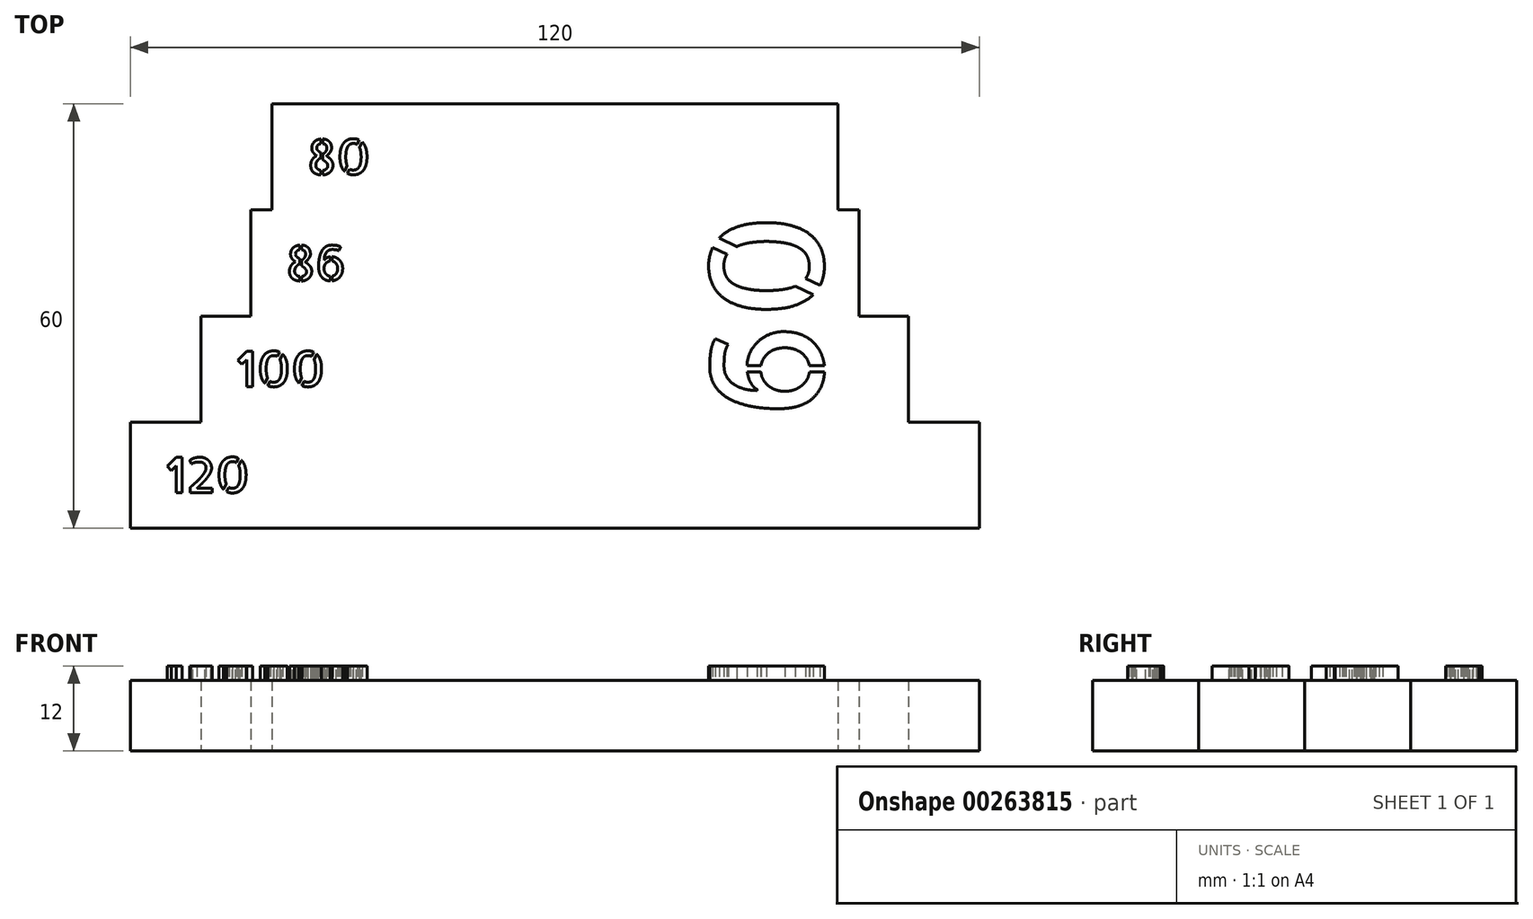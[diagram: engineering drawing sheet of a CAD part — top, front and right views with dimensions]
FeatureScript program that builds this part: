
annotation { "Feature Type Name" : "Feature", "Feature Type Description" : "" }
export const myFeature = defineFeature(function(context is Context, id is Id, definition is map)
    precondition{}
    {
        {
            var Q0;
            Q0=qCreatedBy(makeId("Top.planeOp"),FACE);
            var sketch = newSketch(context, id + "F0", { "sketchPlane" : qUnion([Q0])});
            skLineSegment(sketch, "E0.top", {"start": v(-60, 15) * mm, "end": v(60, 15) * mm});
            skLineSegment(sketch, "E0.left", {"start": v(-60, 0) * mm, "end": v(-60, 15) * mm});
            skLineSegment(sketch, "E0.right", {"start": v(60, 0) * mm, "end": v(60, 15) * mm});
            skLineSegment(sketch, "E1", {"start": v(60, 0) * mm, "end": v(-60, 0) * mm});
            skPoint(sketch, "E2.middle", {"position": v(0, 0) * mm});
            skPoint(sketch, "E3", {"position": v(0, 10) * mm});
            skPoint(sketch, "E4.endSnap0", {"position": v(0, 15) * mm});
            skPoint(sketch, "E5", {"position": v(-60, 7.5) * mm});
            skLineSegment(sketch, "E6.bottom", {"start": v(-50, 30) * mm, "end": v(50, 30) * mm});
            skLineSegment(sketch, "E6.top", {"start": v(-50, 15) * mm, "end": v(50, 15) * mm});
            skLineSegment(sketch, "E6.left", {"start": v(-50, 30) * mm, "end": v(-50, 15) * mm});
            skLineSegment(sketch, "E6.right", {"start": v(50, 30) * mm, "end": v(50, 15) * mm});
            skLineSegment(sketch, "E7.bottom", {"start": v(-43, 30) * mm, "end": v(43, 30) * mm});
            skLineSegment(sketch, "E7.top", {"start": v(-43, 45) * mm, "end": v(43, 45) * mm});
            skLineSegment(sketch, "E7.left", {"start": v(-43, 30) * mm, "end": v(-43, 45) * mm});
            skLineSegment(sketch, "E7.right", {"start": v(43, 30) * mm, "end": v(43, 45) * mm});
            skPoint(sketch, "E8", {"position": v(0, 30) * mm});
            skLineSegment(sketch, "E9.bottom", {"start": v(-40, 45) * mm, "end": v(40, 45) * mm});
            skLineSegment(sketch, "E9.top", {"start": v(-40, 60) * mm, "end": v(40, 60) * mm});
            skLineSegment(sketch, "E9.left", {"start": v(-40, 45) * mm, "end": v(-40, 60) * mm});
            skLineSegment(sketch, "E9.right", {"start": v(40, 45) * mm, "end": v(40, 60) * mm});
            skPoint(sketch, "E10", {"position": v(0, 45) * mm});
            skSolve(sketch);
        }
        {
            var Q0;
            Q0=qSketchRegion(id+"F0",true);
            extrude(context, id + "F1", {"entities" : qUnion([Q0]), "depth" : 10 * mm});
        }
        {
            var Q0;
            Q0=makeQuery(id+"F1.opExtrude","CAP_FACE",FACE,{"disambiguationData":[OSD([sQuery(id+"F0.wireOp",EDGE,"E0.top"),sQuery(id+"F0.wireOp",EDGE,"E0.left"),sQuery(id+"F0.wireOp",EDGE,"E0.right"),sQuery(id+"F0.wireOp",EDGE,"E2.bottom"),sQuery(id+"F0.wireOp",EDGE,"E2.top"),sQuery(id+"F0.wireOp",EDGE,"E2.left"),sQuery(id+"F0.wireOp",EDGE,"E2.right"),sQuery(id+"F0.wireOp",EDGE,"b55eea4f-ecd7-418c-8d86-c4403fabcb0e.sketch_text.stroke-0"),sQuery(id+"F0.wireOp",EDGE,"b55eea4f-ecd7-418c-8d86-c4403fabcb0e.sketch_text.stroke-1"),sQuery(id+"F0.wireOp",EDGE,"b55eea4f-ecd7-418c-8d86-c4403fabcb0e.sketch_text.stroke-2"),sQuery(id+"F0.wireOp",EDGE,"b55eea4f-ecd7-418c-8d86-c4403fabcb0e.sketch_text.stroke-3"),sQuery(id+"F0.wireOp",EDGE,"b55eea4f-ecd7-418c-8d86-c4403fabcb0e.sketch_text.stroke-4"),sQuery(id+"F0.wireOp",EDGE,"b55eea4f-ecd7-418c-8d86-c4403fabcb0e.sketch_text.stroke-5"),sQuery(id+"F0.wireOp",EDGE,"b55eea4f-ecd7-418c-8d86-c4403fabcb0e.sketch_text.stroke-6"),sQuery(id+"F0.wireOp",EDGE,"b55eea4f-ecd7-418c-8d86-c4403fabcb0e.sketch_text.stroke-7"),sQuery(id+"F0.wireOp",EDGE,"b55eea4f-ecd7-418c-8d86-c4403fabcb0e.sketch_text.stroke-8"),sQuery(id+"F0.wireOp",EDGE,"b55eea4f-ecd7-418c-8d86-c4403fabcb0e.sketch_text.stroke-9"),sQuery(id+"F0.wireOp",EDGE,"b55eea4f-ecd7-418c-8d86-c4403fabcb0e.sketch_text.stroke-10"),sQuery(id+"F0.wireOp",EDGE,"b55eea4f-ecd7-418c-8d86-c4403fabcb0e.sketch_text.stroke-11"),sQuery(id+"F0.wireOp",EDGE,"b55eea4f-ecd7-418c-8d86-c4403fabcb0e.sketch_text.stroke-12"),sQuery(id+"F0.wireOp",EDGE,"b55eea4f-ecd7-418c-8d86-c4403fabcb0e.sketch_text.stroke-13"),sQuery(id+"F0.wireOp",EDGE,"b55eea4f-ecd7-418c-8d86-c4403fabcb0e.sketch_text.stroke-14"),sQuery(id+"F0.wireOp",EDGE,"b55eea4f-ecd7-418c-8d86-c4403fabcb0e.sketch_text.stroke-15"),sQuery(id+"F0.wireOp",EDGE,"b55eea4f-ecd7-418c-8d86-c4403fabcb0e.sketch_text.stroke-16"),sQuery(id+"F0.wireOp",EDGE,"b55eea4f-ecd7-418c-8d86-c4403fabcb0e.sketch_text.stroke-17"),sQuery(id+"F0.wireOp",EDGE,"b55eea4f-ecd7-418c-8d86-c4403fabcb0e.sketch_text.stroke-18"),sQuery(id+"F0.wireOp",EDGE,"b55eea4f-ecd7-418c-8d86-c4403fabcb0e.sketch_text.stroke-19"),sQuery(id+"F0.wireOp",EDGE,"b55eea4f-ecd7-418c-8d86-c4403fabcb0e.sketch_text.stroke-20"),sQuery(id+"F0.wireOp",EDGE,"b55eea4f-ecd7-418c-8d86-c4403fabcb0e.sketch_text.stroke-21"),sQuery(id+"F0.wireOp",EDGE,"b55eea4f-ecd7-418c-8d86-c4403fabcb0e.sketch_text.stroke-22"),sQuery(id+"F0.wireOp",EDGE,"b55eea4f-ecd7-418c-8d86-c4403fabcb0e.sketch_text.stroke-23"),sQuery(id+"F0.wireOp",EDGE,"b55eea4f-ecd7-418c-8d86-c4403fabcb0e.sketch_text.stroke-24"),sQuery(id+"F0.wireOp",EDGE,"b55eea4f-ecd7-418c-8d86-c4403fabcb0e.sketch_text.stroke-25"),sQuery(id+"F0.wireOp",EDGE,"b55eea4f-ecd7-418c-8d86-c4403fabcb0e.sketch_text.stroke-26"),sQuery(id+"F0.wireOp",EDGE,"b55eea4f-ecd7-418c-8d86-c4403fabcb0e.sketch_text.stroke-27"),sQuery(id+"F0.wireOp",EDGE,"b55eea4f-ecd7-418c-8d86-c4403fabcb0e.sketch_text.stroke-28"),sQuery(id+"F0.wireOp",EDGE,"b55eea4f-ecd7-418c-8d86-c4403fabcb0e.sketch_text.stroke-29"),sQuery(id+"F0.wireOp",EDGE,"b55eea4f-ecd7-418c-8d86-c4403fabcb0e.sketch_text.stroke-30"),sQuery(id+"F0.wireOp",EDGE,"b55eea4f-ecd7-418c-8d86-c4403fabcb0e.sketch_text.stroke-31"),sQuery(id+"F0.wireOp",EDGE,"b55eea4f-ecd7-418c-8d86-c4403fabcb0e.sketch_text.stroke-32"),sQuery(id+"F0.wireOp",EDGE,"b55eea4f-ecd7-418c-8d86-c4403fabcb0e.sketch_text.stroke-33"),sQuery(id+"F0.wireOp",EDGE,"b55eea4f-ecd7-418c-8d86-c4403fabcb0e.sketch_text.stroke-34"),sQuery(id+"F0.wireOp",EDGE,"b55eea4f-ecd7-418c-8d86-c4403fabcb0e.sketch_text.stroke-35"),sQuery(id+"F0.wireOp",EDGE,"b55eea4f-ecd7-418c-8d86-c4403fabcb0e.sketch_text.stroke-36"),sQuery(id+"F0.wireOp",EDGE,"b55eea4f-ecd7-418c-8d86-c4403fabcb0e.sketch_text.stroke-37"),sQuery(id+"F0.wireOp",EDGE,"b55eea4f-ecd7-418c-8d86-c4403fabcb0e.sketch_text.stroke-38"),sQuery(id+"F0.wireOp",EDGE,"b55eea4f-ecd7-418c-8d86-c4403fabcb0e.sketch_text.stroke-39"),sQuery(id+"F0.wireOp",EDGE,"b55eea4f-ecd7-418c-8d86-c4403fabcb0e.sketch_text.stroke-40"),sQuery(id+"F0.wireOp",EDGE,"b55eea4f-ecd7-418c-8d86-c4403fabcb0e.sketch_text.stroke-41"),sQuery(id+"F0.wireOp",EDGE,"b55eea4f-ecd7-418c-8d86-c4403fabcb0e.sketch_text.stroke-42"),sQuery(id+"F0.wireOp",EDGE,"b55eea4f-ecd7-418c-8d86-c4403fabcb0e.sketch_text.stroke-43"),sQuery(id+"F0.wireOp",EDGE,"b55eea4f-ecd7-418c-8d86-c4403fabcb0e.sketch_text.stroke-44"),sQuery(id+"F0.wireOp",EDGE,"b55eea4f-ecd7-418c-8d86-c4403fabcb0e.sketch_text.stroke-45"),sQuery(id+"F0.wireOp",EDGE,"b55eea4f-ecd7-418c-8d86-c4403fabcb0e.sketch_text.stroke-46"),sQuery(id+"F0.wireOp",EDGE,"b55eea4f-ecd7-418c-8d86-c4403fabcb0e.sketch_text.stroke-47"),sQuery(id+"F0.wireOp",EDGE,"b55eea4f-ecd7-418c-8d86-c4403fabcb0e.sketch_text.stroke-48"),sQuery(id+"F0.wireOp",EDGE,"b55eea4f-ecd7-418c-8d86-c4403fabcb0e.sketch_text.stroke-49"),sQuery(id+"F0.wireOp",EDGE,"b55eea4f-ecd7-418c-8d86-c4403fabcb0e.sketch_text.stroke-50"),sQuery(id+"F0.wireOp",EDGE,"b55eea4f-ecd7-418c-8d86-c4403fabcb0e.sketch_text.stroke-51"),sQuery(id+"F0.wireOp",EDGE,"b55eea4f-ecd7-418c-8d86-c4403fabcb0e.sketch_text.stroke-52"),sQuery(id+"F0.wireOp",EDGE,"b55eea4f-ecd7-418c-8d86-c4403fabcb0e.sketch_text.stroke-53"),sQuery(id+"F0.wireOp",EDGE,"b55eea4f-ecd7-418c-8d86-c4403fabcb0e.sketch_text.stroke-54"),sQuery(id+"F0.wireOp",EDGE,"b55eea4f-ecd7-418c-8d86-c4403fabcb0e.sketch_text.stroke-55"),sQuery(id+"F0.wireOp",EDGE,"b55eea4f-ecd7-418c-8d86-c4403fabcb0e.sketch_text.stroke-56"),sQuery(id+"F0.wireOp",EDGE,"b55eea4f-ecd7-418c-8d86-c4403fabcb0e.sketch_text.stroke-57"),sQuery(id+"F0.wireOp",EDGE,"b55eea4f-ecd7-418c-8d86-c4403fabcb0e.sketch_text.stroke-58"),sQuery(id+"F0.wireOp",EDGE,"b55eea4f-ecd7-418c-8d86-c4403fabcb0e.sketch_text.stroke-59"),sQuery(id+"F0.wireOp",EDGE,"b55eea4f-ecd7-418c-8d86-c4403fabcb0e.sketch_text.stroke-60"),sQuery(id+"F0.wireOp",EDGE,"b55eea4f-ecd7-418c-8d86-c4403fabcb0e.sketch_text.stroke-61"),sQuery(id+"F0.wireOp",EDGE,"b55eea4f-ecd7-418c-8d86-c4403fabcb0e.sketch_text.stroke-62"),sQuery(id+"F0.wireOp",EDGE,"b55eea4f-ecd7-418c-8d86-c4403fabcb0e.sketch_text.stroke-63"),sQuery(id+"F0.wireOp",EDGE,"b55eea4f-ecd7-418c-8d86-c4403fabcb0e.sketch_text.stroke-64"),sQuery(id+"F0.wireOp",EDGE,"b55eea4f-ecd7-418c-8d86-c4403fabcb0e.sketch_text.stroke-65"),sQuery(id+"F0.wireOp",EDGE,"b55eea4f-ecd7-418c-8d86-c4403fabcb0e.sketch_text.stroke-66"),sQuery(id+"F0.wireOp",EDGE,"b55eea4f-ecd7-418c-8d86-c4403fabcb0e.sketch_text.stroke-67"),sQuery(id+"F0.wireOp",EDGE,"b55eea4f-ecd7-418c-8d86-c4403fabcb0e.sketch_text.stroke-68"),sQuery(id+"F0.wireOp",EDGE,"b55eea4f-ecd7-418c-8d86-c4403fabcb0e.sketch_text.stroke-69"),sQuery(id+"F0.wireOp",EDGE,"b55eea4f-ecd7-418c-8d86-c4403fabcb0e.sketch_text.stroke-70"),sQuery(id+"F0.wireOp",EDGE,"b55eea4f-ecd7-418c-8d86-c4403fabcb0e.sketch_text.stroke-71"),sQuery(id+"F0.wireOp",EDGE,"b55eea4f-ecd7-418c-8d86-c4403fabcb0e.sketch_text.stroke-72"),sQuery(id+"F0.wireOp",EDGE,"b55eea4f-ecd7-418c-8d86-c4403fabcb0e.sketch_text.stroke-73"),sQuery(id+"F0.wireOp",EDGE,"b55eea4f-ecd7-418c-8d86-c4403fabcb0e.sketch_text.stroke-74"),sQuery(id+"F0.wireOp",EDGE,"b55eea4f-ecd7-418c-8d86-c4403fabcb0e.sketch_text.stroke-75"),sQuery(id+"F0.wireOp",EDGE,"b55eea4f-ecd7-418c-8d86-c4403fabcb0e.sketch_text.stroke-76"),sQuery(id+"F0.wireOp",EDGE,"b55eea4f-ecd7-418c-8d86-c4403fabcb0e.sketch_text.stroke-77"),sQuery(id+"F0.wireOp",EDGE,"b55eea4f-ecd7-418c-8d86-c4403fabcb0e.sketch_text.stroke-78"),sQuery(id+"F0.wireOp",EDGE,"b55eea4f-ecd7-418c-8d86-c4403fabcb0e.sketch_text.stroke-79"),sQuery(id+"F0.wireOp",EDGE,"b55eea4f-ecd7-418c-8d86-c4403fabcb0e.sketch_text.stroke-80"),sQuery(id+"F0.wireOp",EDGE,"b55eea4f-ecd7-418c-8d86-c4403fabcb0e.sketch_text.stroke-81"),sQuery(id+"F0.wireOp",EDGE,"b55eea4f-ecd7-418c-8d86-c4403fabcb0e.sketch_text.stroke-82"),sQuery(id+"F0.wireOp",EDGE,"b55eea4f-ecd7-418c-8d86-c4403fabcb0e.sketch_text.stroke-83"),sQuery(id+"F0.wireOp",EDGE,"b55eea4f-ecd7-418c-8d86-c4403fabcb0e.sketch_text.stroke-84"),sQuery(id+"F0.wireOp",EDGE,"b55eea4f-ecd7-418c-8d86-c4403fabcb0e.sketch_text.stroke-85"),sQuery(id+"F0.wireOp",EDGE,"b55eea4f-ecd7-418c-8d86-c4403fabcb0e.sketch_text.stroke-86"),sQuery(id+"F0.wireOp",EDGE,"b55eea4f-ecd7-418c-8d86-c4403fabcb0e.sketch_text.stroke-87"),sQuery(id+"F0.wireOp",EDGE,"b55eea4f-ecd7-418c-8d86-c4403fabcb0e.sketch_text.stroke-88"),sQuery(id+"F0.wireOp",EDGE,"b55eea4f-ecd7-418c-8d86-c4403fabcb0e.sketch_text.stroke-89"),sQuery(id+"F0.wireOp",EDGE,"b55eea4f-ecd7-418c-8d86-c4403fabcb0e.sketch_text.stroke-90"),sQuery(id+"F0.wireOp",EDGE,"b55eea4f-ecd7-418c-8d86-c4403fabcb0e.sketch_text.stroke-91"),sQuery(id+"F0.wireOp",EDGE,"b55eea4f-ecd7-418c-8d86-c4403fabcb0e.sketch_text.stroke-92"),sQuery(id+"F0.wireOp",EDGE,"b55eea4f-ecd7-418c-8d86-c4403fabcb0e.sketch_text.stroke-93"),sQuery(id+"F0.wireOp",EDGE,"b55eea4f-ecd7-418c-8d86-c4403fabcb0e.sketch_text.stroke-94"),sQuery(id+"F0.wireOp",EDGE,"b55eea4f-ecd7-418c-8d86-c4403fabcb0e.sketch_text.stroke-95"),sQuery(id+"F0.wireOp",EDGE,"b55eea4f-ecd7-418c-8d86-c4403fabcb0e.sketch_text.stroke-96"),sQuery(id+"F0.wireOp",EDGE,"b55eea4f-ecd7-418c-8d86-c4403fabcb0e.sketch_text.stroke-97"),sQuery(id+"F0.wireOp",EDGE,"b55eea4f-ecd7-418c-8d86-c4403fabcb0e.sketch_text.stroke-98"),sQuery(id+"F0.wireOp",EDGE,"b55eea4f-ecd7-418c-8d86-c4403fabcb0e.sketch_text.stroke-99"),sQuery(id+"F0.wireOp",EDGE,"b55eea4f-ecd7-418c-8d86-c4403fabcb0e.sketch_text.stroke-100"),sQuery(id+"F0.wireOp",EDGE,"b55eea4f-ecd7-418c-8d86-c4403fabcb0e.sketch_text.stroke-101"),sQuery(id+"F0.wireOp",EDGE,"b55eea4f-ecd7-418c-8d86-c4403fabcb0e.sketch_text.stroke-102"),sQuery(id+"F0.wireOp",EDGE,"b55eea4f-ecd7-418c-8d86-c4403fabcb0e.sketch_text.stroke-103"),sQuery(id+"F0.wireOp",EDGE,"b55eea4f-ecd7-418c-8d86-c4403fabcb0e.sketch_text.stroke-104"),sQuery(id+"F0.wireOp",EDGE,"b55eea4f-ecd7-418c-8d86-c4403fabcb0e.sketch_text.stroke-105"),sQuery(id+"F0.wireOp",EDGE,"b55eea4f-ecd7-418c-8d86-c4403fabcb0e.sketch_text.stroke-106"),sQuery(id+"F0.wireOp",EDGE,"b55eea4f-ecd7-418c-8d86-c4403fabcb0e.sketch_text.stroke-107"),sQuery(id+"F0.wireOp",EDGE,"b55eea4f-ecd7-418c-8d86-c4403fabcb0e.sketch_text.stroke-108"),sQuery(id+"F0.wireOp",EDGE,"b55eea4f-ecd7-418c-8d86-c4403fabcb0e.sketch_text.stroke-109"),sQuery(id+"F0.wireOp",EDGE,"b55eea4f-ecd7-418c-8d86-c4403fabcb0e.sketch_text.stroke-110"),sQuery(id+"F0.wireOp",EDGE,"09ea4a2c-0fe9-4a28-b686-1105fd39f020.sketch_text.stroke-0"),sQuery(id+"F0.wireOp",EDGE,"09ea4a2c-0fe9-4a28-b686-1105fd39f020.sketch_text.stroke-1"),sQuery(id+"F0.wireOp",EDGE,"09ea4a2c-0fe9-4a28-b686-1105fd39f020.sketch_text.stroke-2"),sQuery(id+"F0.wireOp",EDGE,"09ea4a2c-0fe9-4a28-b686-1105fd39f020.sketch_text.stroke-3"),sQuery(id+"F0.wireOp",EDGE,"09ea4a2c-0fe9-4a28-b686-1105fd39f020.sketch_text.stroke-4"),sQuery(id+"F0.wireOp",EDGE,"09ea4a2c-0fe9-4a28-b686-1105fd39f020.sketch_text.stroke-5"),sQuery(id+"F0.wireOp",EDGE,"09ea4a2c-0fe9-4a28-b686-1105fd39f020.sketch_text.stroke-6"),sQuery(id+"F0.wireOp",EDGE,"09ea4a2c-0fe9-4a28-b686-1105fd39f020.sketch_text.stroke-7"),sQuery(id+"F0.wireOp",EDGE,"09ea4a2c-0fe9-4a28-b686-1105fd39f020.sketch_text.stroke-8"),sQuery(id+"F0.wireOp",EDGE,"09ea4a2c-0fe9-4a28-b686-1105fd39f020.sketch_text.stroke-9"),sQuery(id+"F0.wireOp",EDGE,"09ea4a2c-0fe9-4a28-b686-1105fd39f020.sketch_text.stroke-10"),sQuery(id+"F0.wireOp",EDGE,"09ea4a2c-0fe9-4a28-b686-1105fd39f020.sketch_text.stroke-11"),sQuery(id+"F0.wireOp",EDGE,"09ea4a2c-0fe9-4a28-b686-1105fd39f020.sketch_text.stroke-12"),sQuery(id+"F0.wireOp",EDGE,"09ea4a2c-0fe9-4a28-b686-1105fd39f020.sketch_text.stroke-13"),sQuery(id+"F0.wireOp",EDGE,"09ea4a2c-0fe9-4a28-b686-1105fd39f020.sketch_text.stroke-14"),sQuery(id+"F0.wireOp",EDGE,"09ea4a2c-0fe9-4a28-b686-1105fd39f020.sketch_text.stroke-15"),sQuery(id+"F0.wireOp",EDGE,"09ea4a2c-0fe9-4a28-b686-1105fd39f020.sketch_text.stroke-16"),sQuery(id+"F0.wireOp",EDGE,"09ea4a2c-0fe9-4a28-b686-1105fd39f020.sketch_text.stroke-17"),sQuery(id+"F0.wireOp",EDGE,"09ea4a2c-0fe9-4a28-b686-1105fd39f020.sketch_text.stroke-18"),sQuery(id+"F0.wireOp",EDGE,"09ea4a2c-0fe9-4a28-b686-1105fd39f020.sketch_text.stroke-19"),sQuery(id+"F0.wireOp",EDGE,"09ea4a2c-0fe9-4a28-b686-1105fd39f020.sketch_text.stroke-20"),sQuery(id+"F0.wireOp",EDGE,"09ea4a2c-0fe9-4a28-b686-1105fd39f020.sketch_text.stroke-21"),sQuery(id+"F0.wireOp",EDGE,"09ea4a2c-0fe9-4a28-b686-1105fd39f020.sketch_text.stroke-22"),sQuery(id+"F0.wireOp",EDGE,"09ea4a2c-0fe9-4a28-b686-1105fd39f020.sketch_text.stroke-23"),sQuery(id+"F0.wireOp",EDGE,"09ea4a2c-0fe9-4a28-b686-1105fd39f020.sketch_text.stroke-24"),sQuery(id+"F0.wireOp",EDGE,"09ea4a2c-0fe9-4a28-b686-1105fd39f020.sketch_text.stroke-25"),sQuery(id+"F0.wireOp",EDGE,"09ea4a2c-0fe9-4a28-b686-1105fd39f020.sketch_text.stroke-26"),sQuery(id+"F0.wireOp",EDGE,"09ea4a2c-0fe9-4a28-b686-1105fd39f020.sketch_text.stroke-27"),sQuery(id+"F0.wireOp",EDGE,"09ea4a2c-0fe9-4a28-b686-1105fd39f020.sketch_text.stroke-28"),sQuery(id+"F0.wireOp",EDGE,"09ea4a2c-0fe9-4a28-b686-1105fd39f020.sketch_text.stroke-29"),sQuery(id+"F0.wireOp",EDGE,"09ea4a2c-0fe9-4a28-b686-1105fd39f020.sketch_text.stroke-30"),sQuery(id+"F0.wireOp",EDGE,"09ea4a2c-0fe9-4a28-b686-1105fd39f020.sketch_text.stroke-31"),sQuery(id+"F0.wireOp",EDGE,"09ea4a2c-0fe9-4a28-b686-1105fd39f020.sketch_text.stroke-32"),sQuery(id+"F0.wireOp",EDGE,"09ea4a2c-0fe9-4a28-b686-1105fd39f020.sketch_text.stroke-33"),sQuery(id+"F0.wireOp",EDGE,"09ea4a2c-0fe9-4a28-b686-1105fd39f020.sketch_text.stroke-34"),sQuery(id+"F0.wireOp",EDGE,"09ea4a2c-0fe9-4a28-b686-1105fd39f020.sketch_text.stroke-35"),sQuery(id+"F0.wireOp",EDGE,"09ea4a2c-0fe9-4a28-b686-1105fd39f020.sketch_text.stroke-36"),sQuery(id+"F0.wireOp",EDGE,"09ea4a2c-0fe9-4a28-b686-1105fd39f020.sketch_text.stroke-37"),sQuery(id+"F0.wireOp",EDGE,"09ea4a2c-0fe9-4a28-b686-1105fd39f020.sketch_text.stroke-38"),sQuery(id+"F0.wireOp",EDGE,"09ea4a2c-0fe9-4a28-b686-1105fd39f020.sketch_text.stroke-39"),sQuery(id+"F0.wireOp",EDGE,"09ea4a2c-0fe9-4a28-b686-1105fd39f020.sketch_text.stroke-40"),sQuery(id+"F0.wireOp",EDGE,"09ea4a2c-0fe9-4a28-b686-1105fd39f020.sketch_text.stroke-41"),sQuery(id+"F0.wireOp",EDGE,"09ea4a2c-0fe9-4a28-b686-1105fd39f020.sketch_text.stroke-42"),sQuery(id+"F0.wireOp",EDGE,"09ea4a2c-0fe9-4a28-b686-1105fd39f020.sketch_text.stroke-43"),sQuery(id+"F0.wireOp",EDGE,"09ea4a2c-0fe9-4a28-b686-1105fd39f020.sketch_text.stroke-44"),sQuery(id+"F0.wireOp",EDGE,"09ea4a2c-0fe9-4a28-b686-1105fd39f020.sketch_text.stroke-45"),sQuery(id+"F0.wireOp",EDGE,"09ea4a2c-0fe9-4a28-b686-1105fd39f020.sketch_text.stroke-46"),sQuery(id+"F0.wireOp",EDGE,"09ea4a2c-0fe9-4a28-b686-1105fd39f020.sketch_text.stroke-47"),sQuery(id+"F0.wireOp",EDGE,"09ea4a2c-0fe9-4a28-b686-1105fd39f020.sketch_text.stroke-48"),sQuery(id+"F0.wireOp",EDGE,"09ea4a2c-0fe9-4a28-b686-1105fd39f020.sketch_text.stroke-49"),sQuery(id+"F0.wireOp",EDGE,"09ea4a2c-0fe9-4a28-b686-1105fd39f020.sketch_text.stroke-50"),sQuery(id+"F0.wireOp",EDGE,"09ea4a2c-0fe9-4a28-b686-1105fd39f020.sketch_text.stroke-51"),sQuery(id+"F0.wireOp",EDGE,"09ea4a2c-0fe9-4a28-b686-1105fd39f020.sketch_text.stroke-52"),sQuery(id+"F0.wireOp",EDGE,"09ea4a2c-0fe9-4a28-b686-1105fd39f020.sketch_text.stroke-53"),sQuery(id+"F0.wireOp",EDGE,"09ea4a2c-0fe9-4a28-b686-1105fd39f020.sketch_text.stroke-54"),sQuery(id+"F0.wireOp",EDGE,"09ea4a2c-0fe9-4a28-b686-1105fd39f020.sketch_text.stroke-55"),sQuery(id+"F0.wireOp",EDGE,"09ea4a2c-0fe9-4a28-b686-1105fd39f020.sketch_text.stroke-56"),sQuery(id+"F0.wireOp",EDGE,"09ea4a2c-0fe9-4a28-b686-1105fd39f020.sketch_text.stroke-57"),sQuery(id+"F0.wireOp",EDGE,"09ea4a2c-0fe9-4a28-b686-1105fd39f020.sketch_text.stroke-58"),sQuery(id+"F0.wireOp",EDGE,"09ea4a2c-0fe9-4a28-b686-1105fd39f020.sketch_text.stroke-59"),sQuery(id+"F0.wireOp",EDGE,"09ea4a2c-0fe9-4a28-b686-1105fd39f020.sketch_text.stroke-60"),sQuery(id+"F0.wireOp",EDGE,"09ea4a2c-0fe9-4a28-b686-1105fd39f020.sketch_text.stroke-61"),sQuery(id+"F0.wireOp",EDGE,"09ea4a2c-0fe9-4a28-b686-1105fd39f020.sketch_text.stroke-62"),sQuery(id+"F0.wireOp",EDGE,"09ea4a2c-0fe9-4a28-b686-1105fd39f020.sketch_text.stroke-63"),sQuery(id+"F0.wireOp",EDGE,"09ea4a2c-0fe9-4a28-b686-1105fd39f020.sketch_text.stroke-64"),sQuery(id+"F0.wireOp",EDGE,"09ea4a2c-0fe9-4a28-b686-1105fd39f020.sketch_text.stroke-65"),sQuery(id+"F0.wireOp",EDGE,"09ea4a2c-0fe9-4a28-b686-1105fd39f020.sketch_text.stroke-66"),sQuery(id+"F0.wireOp",EDGE,"09ea4a2c-0fe9-4a28-b686-1105fd39f020.sketch_text.stroke-67"),sQuery(id+"F0.wireOp",EDGE,"09ea4a2c-0fe9-4a28-b686-1105fd39f020.sketch_text.stroke-68"),sQuery(id+"F0.wireOp",EDGE,"09ea4a2c-0fe9-4a28-b686-1105fd39f020.sketch_text.stroke-69"),sQuery(id+"F0.wireOp",EDGE,"09ea4a2c-0fe9-4a28-b686-1105fd39f020.sketch_text.stroke-70"),sQuery(id+"F0.wireOp",EDGE,"09ea4a2c-0fe9-4a28-b686-1105fd39f020.sketch_text.stroke-71"),sQuery(id+"F0.wireOp",EDGE,"09ea4a2c-0fe9-4a28-b686-1105fd39f020.sketch_text.stroke-72")])],"isStart":false});
            var sketch = newSketch(context, id + "F2", { "sketchPlane" : qUnion([Q0])});
            skText(sketch, "E11", { "text": "86", "fontName": "AllertaStencil-Regular.ttf"});
            skPoint(sketch, "E12", {"position": v(-29.52, 37.5) * mm});
            skText(sketch, "E13", { "text": "120", "fontName": "AllertaStencil-Regular.ttf"});
            skPoint(sketch, "E14", {"position": v(-43.17, 7.5) * mm});
            skText(sketch, "E15", { "text": "100", "fontName": "AllertaStencil-Regular.ttf"});
            skPoint(sketch, "E16", {"position": v(-32.51, 22.5) * mm});
            skText(sketch, "E17", { "text": "60", "fontName": "AllertaStencil-Regular.ttf"});
            skPoint(sketch, "E18", {"position": v(30, 44.69) * mm});
            skLineSegment(sketch, "E19", {"start": v(0, -12.5) * mm, "end": v(60, -12.5) * mm, "construction": true});
            skPoint(sketch, "E19.startSnap0", {"position": v(0, 0) * mm});
            skPoint(sketch, "E20", {"position": v(30, -12.5) * mm});
            skPoint(sketch, "E21", {"position": v(-50, 30) * mm});
            skText(sketch, "E22", { "text": "80", "fontName": "AllertaStencil-Regular.ttf"});
            skPoint(sketch, "E23", {"position": v(-26.09, 52.5) * mm});
            const initialGuessF2  = {"E11": [-0.038, 0.035, 1, 0, 0.005], "E13": [-0.055, 0.005, 1, 0, 0.005], "E15": [-0.045, 0.02, 1, 0, 0.005], "E17": [0.038, 0.01531, 0, 1, 0.016], "E22": [-0.035, 0.05, 1, 0, 0.005]};
            skSetInitialGuess(sketch, initialGuessF2);
            skSolve(sketch);
        }
        {
            var Q0;
            Q0=qSketchRegion(id+"F2",true);
            extrude(context, id + "F3", {"entities" : qUnion([Q0]), "operationType" : NewBodyOperationType.ADD, "depth" : 2 * mm});
        }
    });
